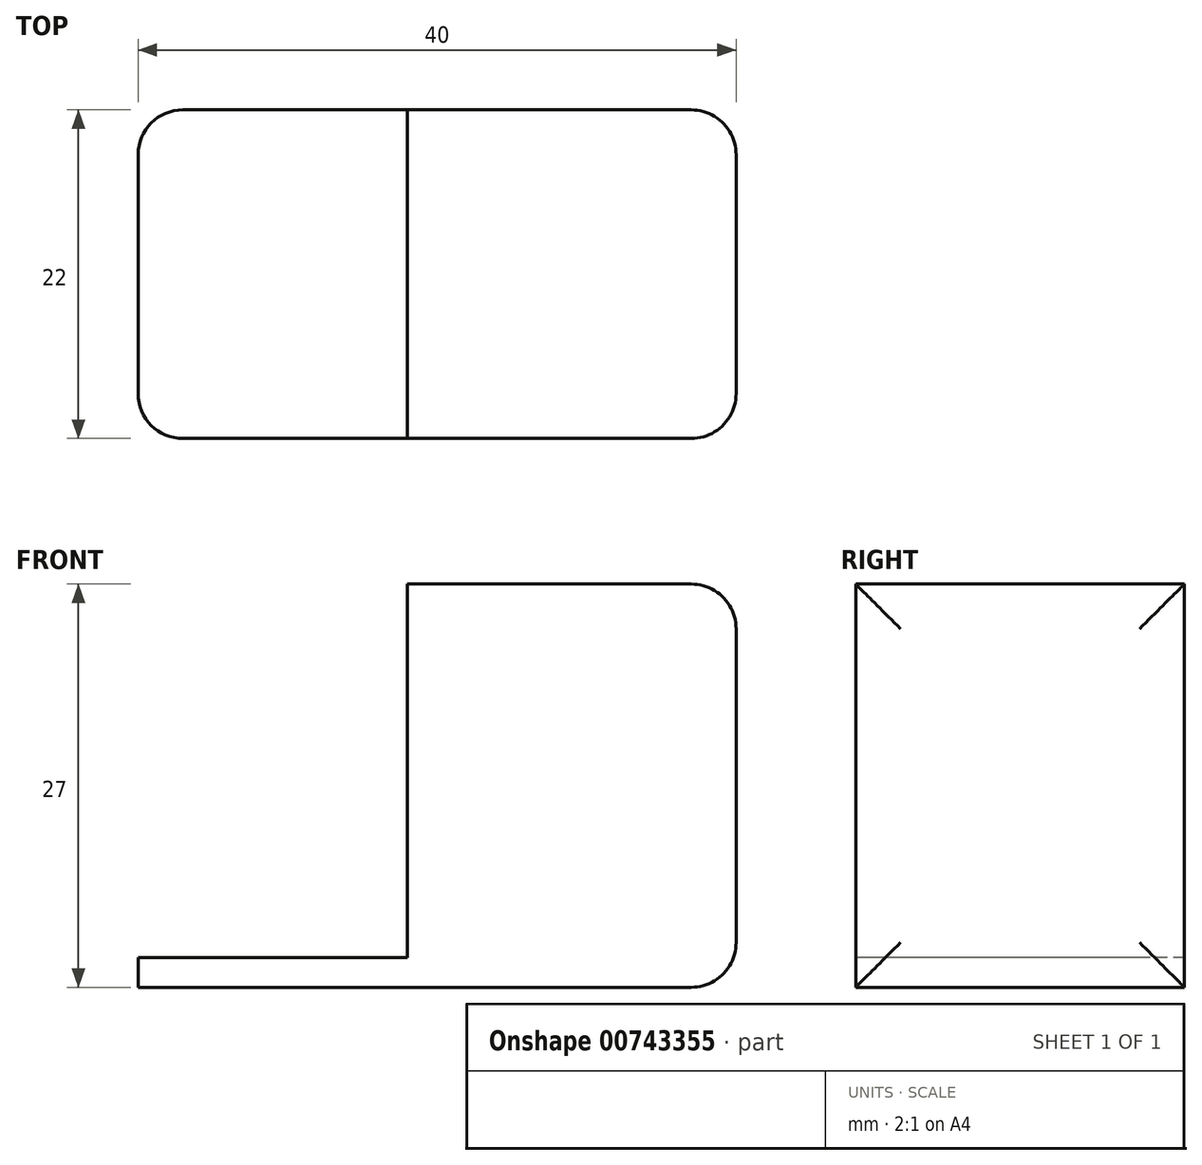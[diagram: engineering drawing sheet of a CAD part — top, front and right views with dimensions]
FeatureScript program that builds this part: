
annotation { "Feature Type Name" : "Feature", "Feature Type Description" : "" }
export const myFeature = defineFeature(function(context is Context, id is Id, definition is map)
    precondition{}
    {
        {
            var Q0;
            Q0=qCreatedBy(makeId("Top.planeOp"),FACE);
            var sketch = newSketch(context, id + "F0", { "sketchPlane" : qUnion([Q0])});
            skLineSegment(sketch, "E0.bottom", {"start": v(-24.8, 11.46) * mm, "end": v(15.2, 11.46) * mm});
            skLineSegment(sketch, "E0.top", {"start": v(-24.8, -10.54) * mm, "end": v(15.2, -10.54) * mm});
            skLineSegment(sketch, "E0.left", {"start": v(-24.8, 11.46) * mm, "end": v(-24.8, -10.54) * mm});
            skLineSegment(sketch, "E0.right", {"start": v(15.2, 11.46) * mm, "end": v(15.2, -10.54) * mm});
            skSolve(sketch);
        }
        {
            var Q0;
            Q0=makeQuery(id+"F0.imprint","IMPRINT",FACE,{"disambiguationData":[TD([[makeQuery(id+"F0.imprint","IMPRINT",EDGE,{"derivedFrom":sQuery(id+"F0.wireOp",EDGE,"E0.bottom")}),-1.0]])]});
            extrude(context, id + "F1", {"entities" : qUnion([Q0]), "depth" : 2 * mm, "offsetDistance" : 25 * mm});
        }
        {
            var Q0;
            Q0=makeQuery(id+"F1.opExtrude","CAP_FACE",FACE,{"disambiguationData":[OSD([sQuery(id+"F0.wireOp",EDGE,"E0.bottom"),sQuery(id+"F0.wireOp",EDGE,"E0.top"),sQuery(id+"F0.wireOp",EDGE,"E0.left"),sQuery(id+"F0.wireOp",EDGE,"E0.right")])],"isStart":false});
            var sketch = newSketch(context, id + "F2", { "sketchPlane" : qUnion([Q0])});
            skLineSegment(sketch, "E1.bottom", {"start": v(15.2, 11.46) * mm, "end": v(-6.8, 11.46) * mm});
            skLineSegment(sketch, "E1.top", {"start": v(15.2, -10.54) * mm, "end": v(-6.8, -10.54) * mm});
            skLineSegment(sketch, "E1.left", {"start": v(15.2, 11.46) * mm, "end": v(15.2, -10.54) * mm});
            skLineSegment(sketch, "E1.right", {"start": v(-6.8, 11.46) * mm, "end": v(-6.8, -10.54) * mm});
            skSolve(sketch);
        }
        {
            var Q0;
            Q0=makeQuery(id+"F2.imprint","IMPRINT",FACE,{"disambiguationData":[TD([[makeQuery(id+"F2.imprint","IMPRINT",EDGE,{"derivedFrom":sQuery(id+"F2.wireOp",EDGE,"E1.bottom")}),-1.0]])]});
            extrude(context, id + "F3", {"entities" : qUnion([Q0]), "operationType" : NewBodyOperationType.ADD, "depth" : 25 * mm, "offsetDistance" : 25 * mm});
        }
        {
            var Q0;
            Q0=makeQuery(id+"F1.opExtrude","SWEPT_EDGE",EDGE,{"disambiguationData":[OSD([sQuery(id+"F0.wireOp",EDGE,"E0.bottom"),sQuery(id+"F0.wireOp",EDGE,"E0.left")])]});
            var Q1;
            Q1=makeQuery(id+"F1.opExtrude","SWEPT_EDGE",EDGE,{"disambiguationData":[OSD([sQuery(id+"F0.wireOp",EDGE,"E0.top"),sQuery(id+"F0.wireOp",EDGE,"E0.left")])]});
            var Q2;
            Q2=makeQuery(id+"F3.boolean.opBoolean","MERGE",EDGE,{"derivedFrom":[makeQuery(id+"F1.opExtrude","SWEPT_EDGE",EDGE,{"disambiguationData":[OSD([sQuery(id+"F0.wireOp",EDGE,"E0.top"),sQuery(id+"F0.wireOp",EDGE,"E0.right")])]}),makeQuery(id+"F3.opExtrude","SWEPT_EDGE",EDGE,{"disambiguationData":[OSD([sQuery(id+"F2.wireOp",EDGE,"E1.top"),sQuery(id+"F2.wireOp",EDGE,"E1.left")])]})]});
            var Q3;
            Q3=makeQuery(id+"F1.opExtrude","CAP_EDGE",EDGE,{"disambiguationData":[OSD([sQuery(id+"F0.wireOp",EDGE,"E0.right")])],"isStart":true});
            var Q4;
            Q4=makeQuery(id+"F3.boolean.opBoolean","MERGE",EDGE,{"derivedFrom":[makeQuery(id+"F1.opExtrude","SWEPT_EDGE",EDGE,{"disambiguationData":[OSD([sQuery(id+"F0.wireOp",EDGE,"E0.bottom"),sQuery(id+"F0.wireOp",EDGE,"E0.right")])]}),makeQuery(id+"F3.opExtrude","SWEPT_EDGE",EDGE,{"disambiguationData":[OSD([sQuery(id+"F2.wireOp",EDGE,"E1.bottom"),sQuery(id+"F2.wireOp",EDGE,"E1.left")])]})]});
            var Q5;
            Q5=makeQuery(id+"F3.opExtrude","CAP_EDGE",EDGE,{"disambiguationData":[OSD([sQuery(id+"F2.wireOp",EDGE,"E1.left")])],"isStart":false});
            fillet(context, id + "F4", {"entities" : qUnion([Q0, Q1, Q2, Q3, Q4, Q5]), "radius" : 3 * mm, "tangentPropagation" : true, "allowEdgeOverflow" : false});
        }
    });
